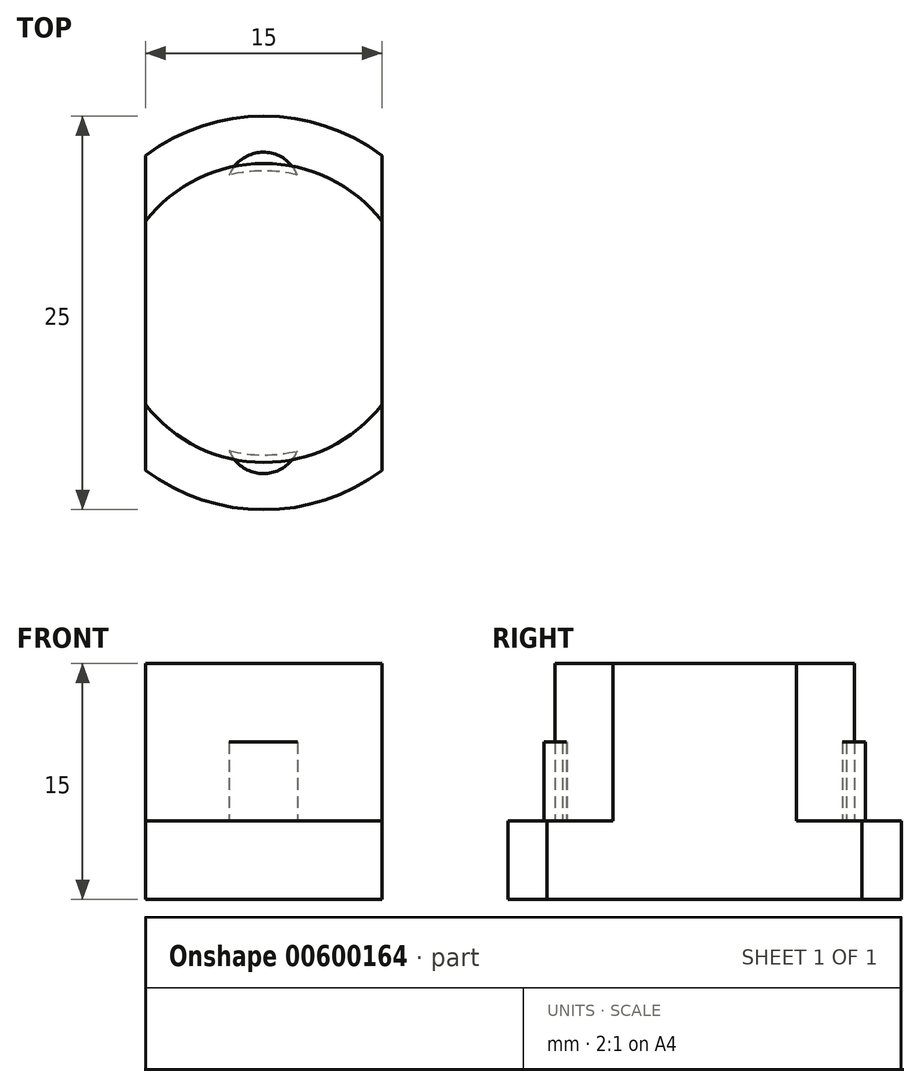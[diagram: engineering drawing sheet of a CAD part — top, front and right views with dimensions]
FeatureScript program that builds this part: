
annotation { "Feature Type Name" : "Feature", "Feature Type Description" : "" }
export const myFeature = defineFeature(function(context is Context, id is Id, definition is map)
    precondition{}
    {
        {
            var Q0;
            Q0=qCreatedBy(makeId("Top.planeOp"),FACE);
            var sketch = newSketch(context, id + "F0", { "sketchPlane" : qUnion([Q0])});
            skCircle(sketch, "E0", {"center": v(0, 0) * mm, "radius": 12.5 * mm});
            skSolve(sketch);
        }
        {
            var Q0;
            Q0=qSketchRegion(id+"F0",true);
            extrude(context, id + "F1", {"entities" : qUnion([Q0]), "oppositeDirection" : true, "depth" : 5 * mm, "offsetDistance" : 25 * mm});
        }
        {
            var Q0;
            Q0=qCreatedBy(makeId("Top.planeOp"),FACE);
            var sketch = newSketch(context, id + "F2", { "sketchPlane" : qUnion([Q0])});
            skCircle(sketch, "E1", {"center": v(0, 0) * mm, "radius": 9.5 * mm});
            skSolve(sketch);
        }
        {
            var Q0;
            Q0=qSketchRegion(id+"F2",true);
            extrude(context, id + "F3", {"entities" : qUnion([Q0]), "operationType" : NewBodyOperationType.ADD, "depth" : 10 * mm, "offsetDistance" : 25 * mm});
        }
        {
            var Q0;
            Q0=qCreatedBy(makeId("Top.planeOp"),FACE);
            var sketch = newSketch(context, id + "F4", { "sketchPlane" : qUnion([Q0])});
            skArc(sketch, "E2", {"start": v(1.01, 8.93) * mm, "mid": v(1, 8.94) * mm, "end": v(1, 8.95) * mm});
            skPoint(sketch, "E3.orphan", {"position": v(0, 9.05) * mm});
            skArc(sketch, "E4", {"start": v(2.13, 8.75) * mm, "mid": v(-0.03, 10.2) * mm, "end": v(-2.2, 8.75) * mm});
            skArc(sketch, "E5", {"start": v(-2.2, 8.75) * mm, "mid": v(-0.03, 9.02) * mm, "end": v(2.13, 8.76) * mm});
            skSolve(sketch);
        }
        {
            var Q0;
            Q0=qSketchRegion(id+"F4",true);
            extrude(context, id + "F5", {"entities" : qUnion([Q0]), "depth" : 5 * mm, "offsetDistance" : 25 * mm});
        }
        {
            var Q0;
            Q0=makeQuery(id+"F5.opExtrude","SWEPT_BODY",BODY,{"disambiguationData":[OSD([sQuery(id+"F4.wireOp",EDGE,"E4"),sQuery(id+"F4.wireOp",EDGE,"E5")])]});
            var Q1;
            Q1=qCreatedBy(makeId("Front.planeOp"),FACE);
            mirror(context, id + "F6", {"entities" : qUnion([Q0]), "mirrorPlane" : qUnion([Q1])});
        }
        {
            var Q0;
            Q0=qCreatedBy(makeId("Top.planeOp"),FACE);
            var sketch = newSketch(context, id + "F7", { "sketchPlane" : qUnion([Q0])});
            skLineSegment(sketch, "E6.bottom", {"start": v(-7.5, -13.5) * mm, "end": v(7.5, -13.5) * mm});
            skLineSegment(sketch, "E6.top", {"start": v(-7.5, 13.5) * mm, "end": v(7.5, 13.5) * mm});
            skLineSegment(sketch, "E6.left", {"start": v(-7.5, -13.5) * mm, "end": v(-7.5, 13.5) * mm});
            skLineSegment(sketch, "E6.right", {"start": v(7.5, -13.5) * mm, "end": v(7.5, 13.5) * mm});
            skPoint(sketch, "E6.middle", {"position": v(0, 0) * mm});
            skLineSegment(sketch, "E7.bottom", {"start": v(-15, -15) * mm, "end": v(15, -15) * mm});
            skLineSegment(sketch, "E7.top", {"start": v(-15, 15) * mm, "end": v(15, 15) * mm});
            skLineSegment(sketch, "E7.left", {"start": v(-15, -15) * mm, "end": v(-15, 15) * mm});
            skLineSegment(sketch, "E7.right", {"start": v(15, -15) * mm, "end": v(15, 15) * mm});
            skSolve(sketch);
        }
        {
            var Q0;
            Q0=qSketchRegion(id+"F7",true);
            extrude(context, id + "F8", {"entities" : qUnion([Q0]), "endBound" : BoundingType.SYMMETRIC, "depth" : 20 * mm, "offsetDistance" : 25 * mm});
        }
        {
            var Q0;
            Q0=makeQuery(id+"F8.opExtrude","SWEPT_BODY",BODY,{"disambiguationData":[OSD([sQuery(id+"F7.wireOp",EDGE,"E6.bottom"),sQuery(id+"F7.wireOp",EDGE,"E6.top"),sQuery(id+"F7.wireOp",EDGE,"E6.left"),sQuery(id+"F7.wireOp",EDGE,"E6.right"),sQuery(id+"F7.wireOp",EDGE,"E7.bottom"),sQuery(id+"F7.wireOp",EDGE,"E7.top"),sQuery(id+"F7.wireOp",EDGE,"E7.left"),sQuery(id+"F7.wireOp",EDGE,"E7.right")])]});
            var Q1;
            Q1=makeQuery(id+"F1.opExtrude","SWEPT_BODY",BODY,{"disambiguationData":[OSD([sQuery(id+"F0.wireOp",EDGE,"E0")])]});
            booleanBodies(context, id + "F9", {"operationType" : BooleanOperationType.SUBTRACTION, "tools" : qUnion([Q0]), "targets" : qUnion([Q1])});
        }
        {
            var Q0;
            Q0=makeQuery(id+"F3.opExtrude","CAP_FACE",FACE,{"disambiguationData":[OSD([sQuery(id+"F2.wireOp",EDGE,"E1")])],"isStart":false});
            var sketch = newSketch(context, id + "F10", { "sketchPlane" : qUnion([Q0])});
            skLineSegment(sketch, "E8.bottom", {"start": v(-9, 12.5) * mm, "end": v(9, 12.5) * mm});
            skLineSegment(sketch, "E8.top", {"start": v(-9, -12.5) * mm, "end": v(9, -12.5) * mm});
            skLineSegment(sketch, "E8.left", {"start": v(-9, 12.5) * mm, "end": v(-9, -12.5) * mm});
            skLineSegment(sketch, "E8.right", {"start": v(9, 12.5) * mm, "end": v(9, -12.5) * mm});
            skPoint(sketch, "E8.middle", {"position": v(0, 0) * mm});
            skSolve(sketch);
        }
        {
            var Q0;
            Q0=makeQuery(id+"F1.opExtrude","CAP_FACE",FACE,{"disambiguationData":[OSD([sQuery(id+"F0.wireOp",EDGE,"E0")])],"isStart":false});
            var sketch = newSketch(context, id + "F11", { "sketchPlane" : qUnion([Q0])});
            skLineSegment(sketch, "E9.bottom", {"start": v(-11.06, 16.38) * mm, "end": v(12.2, 16.38) * mm});
            skLineSegment(sketch, "E9.top", {"start": v(-11.06, -18.83) * mm, "end": v(12.2, -18.83) * mm});
            skLineSegment(sketch, "E9.left", {"start": v(-11.06, 16.38) * mm, "end": v(-11.06, -18.83) * mm});
            skLineSegment(sketch, "E9.right", {"start": v(12.2, 16.38) * mm, "end": v(12.2, -18.83) * mm});
            skLineSegment(sketch, "E10.bottom", {"start": v(-7, 13.5) * mm, "end": v(7, 13.5) * mm});
            skLineSegment(sketch, "E10.top", {"start": v(-7, -13.5) * mm, "end": v(7, -13.5) * mm});
            skLineSegment(sketch, "E10.left", {"start": v(-7, 13.5) * mm, "end": v(-7, -13.5) * mm});
            skLineSegment(sketch, "E10.right", {"start": v(7, 13.5) * mm, "end": v(7, -13.5) * mm});
            skPoint(sketch, "E10.middle", {"position": v(0, 0) * mm});
            skSolve(sketch);
        }
        {
            var Q0;
            Q0=makeQuery(id+"F11.imprint","IMPRINT",FACE,{"disambiguationData":[TD([[makeQuery(id+"F11.imprint","IMPRINT",EDGE,{"derivedFrom":sQuery(id+"F11.wireOp",EDGE,"E9.bottom")}),-1.0]])]});
            extrude(context, id + "F12", {"entities" : qUnion([Q0]), "oppositeDirection" : true, "depth" : 35 * mm, "offsetDistance" : 25 * mm});
        }
        {
            var Q0;
            Q0=makeQuery(id+"F12.opExtrude","SWEPT_BODY",BODY,{"disambiguationData":[OSD([sQuery(id+"F11.wireOp",EDGE,"CsTShpJo-yupG-J2VR-TzQz-PlvGGC6WDBXw"),sQuery(id+"F11.wireOp",EDGE,"PACYzvug-Flbu-Hwa7-5zGb-IofVGRI0exgx"),sQuery(id+"F11.wireOp",EDGE,"SDOYAuIW-NyJX-Uuye-oQSR-vI6YNacnY2Zf"),sQuery(id+"F11.wireOp",EDGE,"Hm5EeVvH-lZfm-I2iu-cQlH-7euyYO7ieHp2"),sQuery(id+"F11.wireOp",EDGE,"E9.bottom"),sQuery(id+"F11.wireOp",EDGE,"E9.top"),sQuery(id+"F11.wireOp",EDGE,"E9.left"),sQuery(id+"F11.wireOp",EDGE,"E9.right")])]});
            var Q1;
            Q1=makeQuery(id+"FxUAvpqGPErD5z1_82.opExtrude","SWEPT_BODY",BODY,{"disambiguationData":[OSD([sQuery(id+"F10.wireOp",EDGE,"E8.bottom"),sQuery(id+"F10.wireOp",EDGE,"E8.top"),sQuery(id+"F10.wireOp",EDGE,"E8.left"),sQuery(id+"F10.wireOp",EDGE,"E8.right")])]});
            var Q2;
            Q2=makeQuery(id+"F6.opPattern","COPY",BODY,{"derivedFrom":makeQuery(id+"F5.opExtrude","SWEPT_BODY",BODY,{"disambiguationData":[OSD([sQuery(id+"F4.wireOp",EDGE,"E4"),sQuery(id+"F4.wireOp",EDGE,"E5")])]}),"instanceName":"1"});
            var Q3;
            Q3=makeQuery(id+"F5.opExtrude","SWEPT_BODY",BODY,{"disambiguationData":[OSD([sQuery(id+"F4.wireOp",EDGE,"E4"),sQuery(id+"F4.wireOp",EDGE,"E5")])]});
            var Q4;
            Q4=makeQuery(id+"F1.opExtrude","SWEPT_BODY",BODY,{"disambiguationData":[OSD([sQuery(id+"F0.wireOp",EDGE,"E0")])]});
            booleanBodies(context, id + "F13", {"operationType" : BooleanOperationType.SUBTRACTION, "tools" : qUnion([Q0]), "targets" : qUnion([Q1, Q2, Q3, Q4])});
        }
    });
